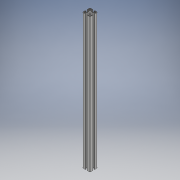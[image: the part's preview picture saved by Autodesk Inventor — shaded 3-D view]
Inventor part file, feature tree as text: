
AUTODESK INVENTOR PART (.ipt)
format: ipt  version: 2019 (Build 230136000, 136)  size: 298,496 bytes
history: native  units: mm
features: extrude x1, sketch x1
ambient origin geometry x8: Origin, YZ Plane, XZ Plane, XY Plane, X Axis, Y Axis, Z Axis, Center Point
bodies: Solid1 (feature_tree)
feature tree (2):
  extrude  "Extrusion1"  Depth=700.0mm
  sketch  "Sketch1"  dims[d0=4.1mm d1=5.1mm d2=6.4mm d3=7.4mm d4=9.25mm d5=10.25mm d6=11.55mm d7=12.55mm d8=15.5mm d9=18.5mm d10=20.0mm d11=17.5mm d12=700.0mm d13=0.0mm d15=6.8mm]
